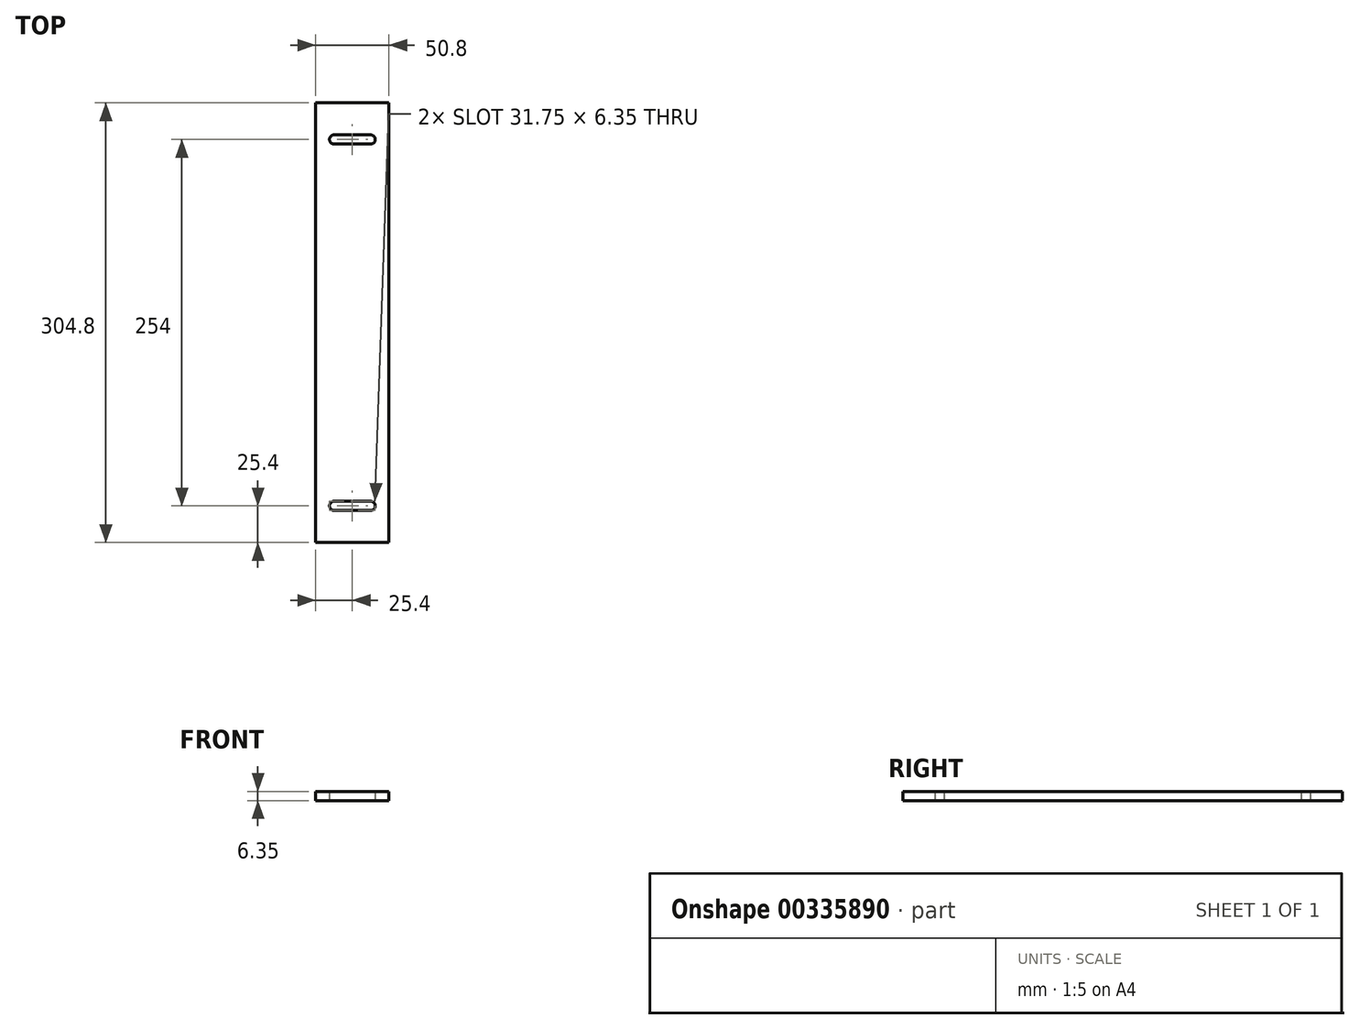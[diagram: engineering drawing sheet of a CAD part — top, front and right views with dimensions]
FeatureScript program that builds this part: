
annotation { "Feature Type Name" : "Feature", "Feature Type Description" : "" }
export const myFeature = defineFeature(function(context is Context, id is Id, definition is map)
    precondition{}
    {
        {
            var Q0;
            Q0=qCreatedBy(makeId("Top.planeOp"),FACE);
            var sketch = newSketch(context, id + "F0", { "sketchPlane" : qUnion([Q0])});
            skLineSegment(sketch, "E0.bottom", {"start": v(-25.4, 152.4) * mm, "end": v(25.4, 152.4) * mm});
            skLineSegment(sketch, "E0.top", {"start": v(-25.4, -152.4) * mm, "end": v(25.4, -152.4) * mm});
            skLineSegment(sketch, "E0.left", {"start": v(-25.4, 152.4) * mm, "end": v(-25.4, -152.4) * mm});
            skLineSegment(sketch, "E0.right", {"start": v(25.4, 152.4) * mm, "end": v(25.4, -152.4) * mm});
            skSolve(sketch);
        }
        {
            var Q0;
            Q0 = qSketchRegion(id + "F0", true);
            extrude(context, id + "F1", {"entities" : qUnion([Q0]), "depth" : 6.35 * mm});
        }
        {
            var Q0;
            Q0=qCreatedBy(makeId("Top.planeOp"),FACE);
            var sketch = newSketch(context, id + "F2", { "sketchPlane" : qUnion([Q0])});
            skLineSegment(sketch, "E1.bottom", {"start": v(-12.7, 130.18) * mm, "end": v(12.7, 130.18) * mm});
            skLineSegment(sketch, "E1.top", {"start": v(-12.7, 123.82) * mm, "end": v(12.7, 123.82) * mm});
            skArc(sketch, "E2", {"start": v(12.7, 123.83) * mm, "mid": v(15.87, 127) * mm, "end": v(12.7, 130.18) * mm});
            skArc(sketch, "E3", {"start": v(-12.7, 130.18) * mm, "mid": v(-15.88, 127) * mm, "end": v(-12.7, 123.82) * mm});
            skLineSegment(sketch, "E4.bottom", {"start": v(-12.7, -123.83) * mm, "end": v(12.7, -123.83) * mm});
            skLineSegment(sketch, "E4.top", {"start": v(-12.7, -130.18) * mm, "end": v(12.7, -130.18) * mm});
            skArc(sketch, "E5", {"start": v(-12.7, -123.82) * mm, "mid": v(-15.88, -127) * mm, "end": v(-12.7, -130.18) * mm});
            skArc(sketch, "E6", {"start": v(12.7, -130.18) * mm, "mid": v(15.88, -127) * mm, "end": v(12.7, -123.83) * mm});
            skSolve(sketch);
        }
        {
            var Q0;
            Q0 = qSketchRegion(id + "F2", true);
            extrude(context, id + "F3", {"entities" : qUnion([Q0]), "operationType" : NewBodyOperationType.REMOVE, "depth" : 25.4 * mm});
        }
    });
